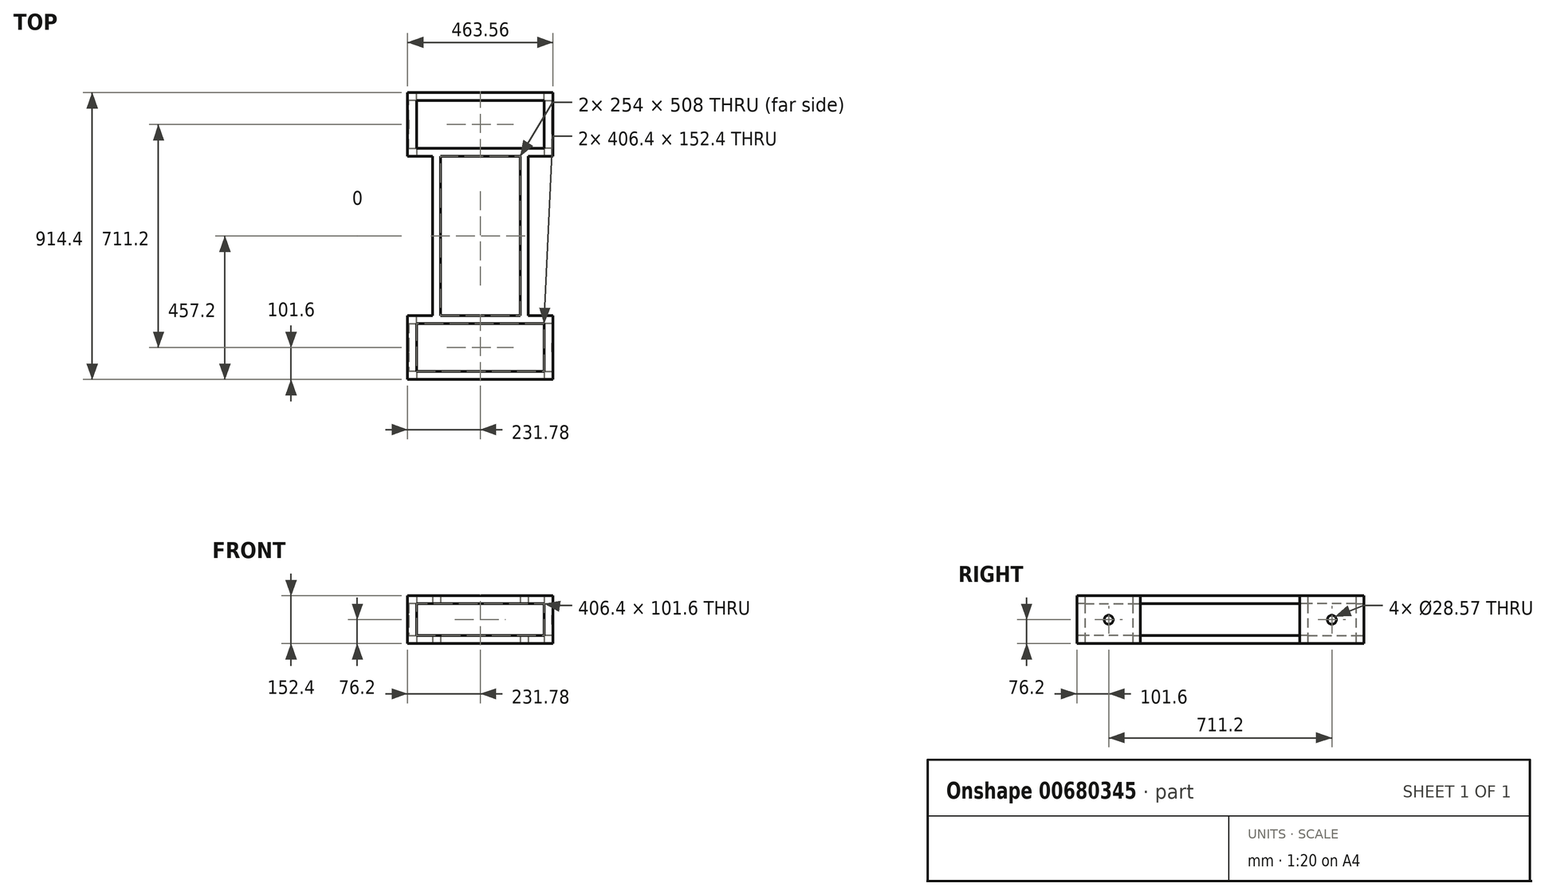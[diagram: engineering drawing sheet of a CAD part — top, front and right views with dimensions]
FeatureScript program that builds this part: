
annotation { "Feature Type Name" : "Feature", "Feature Type Description" : "" }
export const myFeature = defineFeature(function(context is Context, id is Id, definition is map)
    precondition{}
    {
        {
            var Q0;
            Q0=qCreatedBy(makeId("Top.planeOp"),FACE);
            var sketch = newSketch(context, id + "F0", { "sketchPlane" : qUnion([Q0])});
            skLineSegment(sketch, "E0.bottom", {"start": v(-228.6, 457.2) * mm, "end": v(228.6, 457.2) * mm});
            skLineSegment(sketch, "E0.top", {"start": v(-228.6, -457.2) * mm, "end": v(228.6, -457.2) * mm});
            skLineSegment(sketch, "E0.left", {"start": v(-228.6, 457.2) * mm, "end": v(-228.6, -457.2) * mm, "construction": true});
            skLineSegment(sketch, "E0.right", {"start": v(228.6, 457.2) * mm, "end": v(228.6, -457.2) * mm, "construction": true});
            skLineSegment(sketch, "E1.bottom", {"start": v(-203.2, 431.8) * mm, "end": v(203.2, 431.8) * mm});
            skLineSegment(sketch, "E1.top", {"start": v(-203.2, -431.8) * mm, "end": v(203.2, -431.8) * mm});
            skLineSegment(sketch, "E1.left", {"start": v(-203.2, 431.8) * mm, "end": v(-203.2, -431.8) * mm, "construction": true});
            skLineSegment(sketch, "E1.right", {"start": v(203.2, 431.8) * mm, "end": v(203.2, -431.8) * mm, "construction": true});
            skPoint(sketch, "E2", {"position": v(0, 431.8) * mm});
            skPoint(sketch, "E3", {"position": v(0, 457.2) * mm});
            skPoint(sketch, "E4", {"position": v(228.6, 0) * mm});
            skPoint(sketch, "E5", {"position": v(203.2, 0) * mm});
            skLineSegment(sketch, "E6.bottom", {"start": v(-203.2, -279.4) * mm, "end": v(203.2, -279.4) * mm});
            skLineSegment(sketch, "E6.top", {"start": v(-203.2, -254) * mm, "end": v(203.2, -254) * mm});
            skLineSegment(sketch, "E6.left", {"start": v(-203.2, -279.4) * mm, "end": v(-203.2, -254) * mm});
            skLineSegment(sketch, "E6.right", {"start": v(203.2, -279.4) * mm, "end": v(203.2, -254) * mm});
            skLineSegment(sketch, "E7.MirrorCS", {"start": v(-203.2, 254) * mm, "end": v(203.2, 254) * mm});
            skLineSegment(sketch, "E8.MirrorCS", {"start": v(-203.2, 279.4) * mm, "end": v(203.2, 279.4) * mm});
            skLineSegment(sketch, "E9", {"start": v(0, 457.2) * mm, "end": v(0, -457.2) * mm, "construction": true});
            skLineSegment(sketch, "E10.bottom", {"start": v(-152.4, -254) * mm, "end": v(-127, -254) * mm});
            skLineSegment(sketch, "E10.top", {"start": v(-152.4, 254) * mm, "end": v(-127, 254) * mm});
            skLineSegment(sketch, "E10.left", {"start": v(-152.4, -254) * mm, "end": v(-152.4, 254) * mm});
            skLineSegment(sketch, "E10.right", {"start": v(-127, -254) * mm, "end": v(-127, 254) * mm});
            skLineSegment(sketch, "E11.MirrorCS", {"start": v(127, -254) * mm, "end": v(127, 254) * mm});
            skLineSegment(sketch, "E12.MirrorCS", {"start": v(152.4, -254) * mm, "end": v(152.4, 254) * mm});
            skLineSegment(sketch, "E13", {"start": v(-203.2, 254) * mm, "end": v(-228.6, 254) * mm});
            skLineSegment(sketch, "E14", {"start": v(-228.6, 254) * mm, "end": v(-228.6, 457.2) * mm});
            skLineSegment(sketch, "E15", {"start": v(-203.2, 431.8) * mm, "end": v(-203.2, 279.4) * mm});
            skLineSegment(sketch, "E16", {"start": v(-203.2, -254) * mm, "end": v(-228.6, -254) * mm});
            skLineSegment(sketch, "E17", {"start": v(-228.6, -254) * mm, "end": v(-228.6, -457.2) * mm});
            skLineSegment(sketch, "E18", {"start": v(-203.2, -431.8) * mm, "end": v(-203.2, -279.4) * mm});
            skLineSegment(sketch, "E19", {"start": v(203.2, -431.8) * mm, "end": v(203.2, -279.4) * mm});
            skLineSegment(sketch, "E20", {"start": v(203.2, -254) * mm, "end": v(228.6, -254) * mm});
            skLineSegment(sketch, "E21", {"start": v(228.6, -254) * mm, "end": v(228.6, -457.2) * mm});
            skLineSegment(sketch, "E22", {"start": v(203.2, 254) * mm, "end": v(228.6, 254) * mm});
            skLineSegment(sketch, "E23", {"start": v(228.6, 254) * mm, "end": v(228.6, 457.2) * mm});
            skLineSegment(sketch, "E24", {"start": v(203.2, 279.4) * mm, "end": v(203.2, 431.8) * mm});
            skSolve(sketch);
        }
        {
            var Q0;
            Q0=qSketchRegion(id+"F0",true);
            var Q1;
            Q1=makeQuery(id+"F0.imprint","IMPRINT",FACE,{"disambiguationData":[TD([[makeQuery(id+"F0.imprint","IMPRINT",EDGE,{"derivedFrom":sQuery(id+"F0.wireOp",EDGE,"E6.bottom")}),1.0]])]});
            var Q2;
            {var subQ0=sQuery(id+"F0.wireOp",EDGE,"E7.MirrorCS");Q2=makeQuery(id+"F0.imprint","IMPRINT",FACE,{"disambiguationData":[TD([[makeQuery(id+"F0.imprint","IMPRINT",EDGE,{"derivedFrom":subQ0}),1.0]])]});}
            extrude(context, id + "F1", {"entities" : qUnion([Q0, Q1, Q2]), "depth" : 25.4 * mm, "offsetDistance" : 25.4 * mm});
        }
        {
            var Q0;
            Q0=makeQuery(id+"F1.opExtrude","CAP_FACE",FACE,{"disambiguationData":[OSD([sQuery(id+"F0.wireOp",EDGE,"E0.bottom"),sQuery(id+"F0.wireOp",EDGE,"E0.top"),sQuery(id+"F0.wireOp",EDGE,"E0.left"),sQuery(id+"F0.wireOp",EDGE,"E0.right"),sQuery(id+"F0.wireOp",EDGE,"E1.bottom"),sQuery(id+"F0.wireOp",EDGE,"E1.top"),sQuery(id+"F0.wireOp",EDGE,"E1.left"),sQuery(id+"F0.wireOp",EDGE,"E1.right")])],"isStart":false});
            var sketch = newSketch(context, id + "F2", { "sketchPlane" : qUnion([Q0])});
            skLineSegment(sketch, "E25.bottom", {"start": v(-203.2, -431.8) * mm, "end": v(-228.6, -431.8) * mm});
            skLineSegment(sketch, "E25.top", {"start": v(-203.2, -457.2) * mm, "end": v(-228.6, -457.2) * mm});
            skLineSegment(sketch, "E25.left", {"start": v(-203.2, -431.8) * mm, "end": v(-203.2, -457.2) * mm});
            skLineSegment(sketch, "E25.right", {"start": v(-228.6, -431.8) * mm, "end": v(-228.6, -457.2) * mm});
            skLineSegment(sketch, "E26.MirrorCS", {"start": v(-228.6, 431.8) * mm, "end": v(-228.6, 457.2) * mm});
            skLineSegment(sketch, "E27.MirrorCS", {"start": v(-203.2, 431.8) * mm, "end": v(-203.2, 457.2) * mm});
            skLineSegment(sketch, "E28.MirrorCS", {"start": v(-203.2, 457.2) * mm, "end": v(-228.6, 457.2) * mm});
            skLineSegment(sketch, "E29.MirrorCS", {"start": v(-203.2, 431.8) * mm, "end": v(-228.6, 431.8) * mm});
            skLineSegment(sketch, "E30.MirrorCS", {"start": v(203.2, 457.2) * mm, "end": v(228.6, 457.2) * mm});
            skLineSegment(sketch, "E31.MirrorCS", {"start": v(203.2, 431.8) * mm, "end": v(203.2, 457.2) * mm});
            skLineSegment(sketch, "E32.MirrorCS", {"start": v(228.6, 431.8) * mm, "end": v(228.6, 457.2) * mm});
            skLineSegment(sketch, "E33.MirrorCS", {"start": v(228.6, -431.8) * mm, "end": v(228.6, -457.2) * mm});
            skLineSegment(sketch, "E34.MirrorCS", {"start": v(203.2, -431.8) * mm, "end": v(203.2, -457.2) * mm});
            skLineSegment(sketch, "E35.MirrorCS", {"start": v(203.2, -457.2) * mm, "end": v(228.6, -457.2) * mm});
            skLineSegment(sketch, "E36.MirrorCS", {"start": v(203.2, -431.8) * mm, "end": v(228.6, -431.8) * mm});
            skLineSegment(sketch, "E37.MirrorCS", {"start": v(203.2, 431.8) * mm, "end": v(228.6, 431.8) * mm});
            skLineSegment(sketch, "E38.bottom", {"start": v(-228.6, -279.4) * mm, "end": v(-203.2, -279.4) * mm});
            skLineSegment(sketch, "E38.top", {"start": v(-228.6, -254) * mm, "end": v(-203.2, -254) * mm});
            skLineSegment(sketch, "E38.left", {"start": v(-228.6, -279.4) * mm, "end": v(-228.6, -254) * mm});
            skLineSegment(sketch, "E38.right", {"start": v(-203.2, -279.4) * mm, "end": v(-203.2, -254) * mm});
            skLineSegment(sketch, "E39.MirrorCS", {"start": v(-228.6, 279.4) * mm, "end": v(-228.6, 254) * mm});
            skLineSegment(sketch, "E40.MirrorCS", {"start": v(-228.6, 279.4) * mm, "end": v(-203.2, 279.4) * mm});
            skLineSegment(sketch, "E41.MirrorCS", {"start": v(-203.2, 279.4) * mm, "end": v(-203.2, 254) * mm});
            skLineSegment(sketch, "E42.MirrorCS", {"start": v(-228.6, 254) * mm, "end": v(-203.2, 254) * mm});
            skLineSegment(sketch, "E43.MirrorCS", {"start": v(228.6, -254) * mm, "end": v(203.2, -254) * mm});
            skLineSegment(sketch, "E44.MirrorCS", {"start": v(203.2, -279.4) * mm, "end": v(203.2, -254) * mm});
            skLineSegment(sketch, "E45.MirrorCS", {"start": v(228.6, 279.4) * mm, "end": v(203.2, 279.4) * mm});
            skLineSegment(sketch, "E46.MirrorCS", {"start": v(228.6, 254) * mm, "end": v(203.2, 254) * mm});
            skLineSegment(sketch, "E47.MirrorCS", {"start": v(203.2, 279.4) * mm, "end": v(203.2, 254) * mm});
            skLineSegment(sketch, "E48.MirrorCS", {"start": v(228.6, 279.4) * mm, "end": v(228.6, 254) * mm});
            skLineSegment(sketch, "E49.MirrorCS", {"start": v(228.6, -279.4) * mm, "end": v(203.2, -279.4) * mm});
            skLineSegment(sketch, "E50.MirrorCS", {"start": v(228.6, -279.4) * mm, "end": v(228.6, -254) * mm});
            skSolve(sketch);
        }
        {
            var Q0;
            Q0=qSketchRegion(id+"F2",true);
            extrude(context, id + "F3", {"entities" : qUnion([Q0]), "operationType" : NewBodyOperationType.ADD, "depth" : 101.6 * mm, "offsetDistance" : 25.4 * mm});
        }
        {
            var Q0;
            Q0=makeQuery(id+"F3.opExtrude","CAP_FACE",FACE,{"disambiguationData":[OSD([sQuery(id+"F2.wireOp",EDGE,"E33.MirrorCS"),sQuery(id+"F2.wireOp",EDGE,"E34.MirrorCS"),sQuery(id+"F2.wireOp",EDGE,"E35.MirrorCS"),sQuery(id+"F2.wireOp",EDGE,"E36.MirrorCS")])],"isStart":false});
            var sketch = newSketch(context, id + "F4", { "sketchPlane" : qUnion([Q0])});
            skLineSegment(sketch, "E51.bottom", {"start": v(228.6, 457.2) * mm, "end": v(-228.6, 457.2) * mm});
            skLineSegment(sketch, "E51.top", {"start": v(228.6, 431.8) * mm, "end": v(-228.6, 431.8) * mm});
            skLineSegment(sketch, "E51.left", {"start": v(228.6, 457.2) * mm, "end": v(228.6, 431.8) * mm});
            skLineSegment(sketch, "E51.right", {"start": v(-228.6, 457.2) * mm, "end": v(-228.6, 431.8) * mm});
            skLineSegment(sketch, "E52.bottom", {"start": v(228.6, 431.8) * mm, "end": v(203.2, 431.8) * mm});
            skLineSegment(sketch, "E52.top", {"start": v(228.6, 254) * mm, "end": v(203.2, 254) * mm});
            skLineSegment(sketch, "E52.left", {"start": v(228.6, 431.8) * mm, "end": v(228.6, 254) * mm});
            skLineSegment(sketch, "E52.right", {"start": v(203.2, 431.8) * mm, "end": v(203.2, 254) * mm});
            skLineSegment(sketch, "E53.MirrorCS", {"start": v(-203.2, 431.8) * mm, "end": v(-203.2, 254) * mm});
            skLineSegment(sketch, "E54.MirrorCS", {"start": v(-228.6, 431.8) * mm, "end": v(-228.6, 254) * mm});
            skLineSegment(sketch, "E55.MirrorCS", {"start": v(-228.6, 254) * mm, "end": v(-203.2, 254) * mm});
            skLineSegment(sketch, "E56.bottom", {"start": v(203.2, 254) * mm, "end": v(-203.2, 254) * mm});
            skLineSegment(sketch, "E56.top", {"start": v(203.2, 279.4) * mm, "end": v(-203.2, 279.4) * mm});
            skLineSegment(sketch, "E56.left", {"start": v(203.2, 254) * mm, "end": v(203.2, 279.4) * mm});
            skLineSegment(sketch, "E56.right", {"start": v(-203.2, 254) * mm, "end": v(-203.2, 279.4) * mm});
            skLineSegment(sketch, "E57.bottom", {"start": v(152.4, 254) * mm, "end": v(127, 254) * mm});
            skLineSegment(sketch, "E57.top", {"start": v(152.4, -254) * mm, "end": v(127, -254) * mm});
            skLineSegment(sketch, "E57.left", {"start": v(152.4, 254) * mm, "end": v(152.4, -254) * mm});
            skLineSegment(sketch, "E57.right", {"start": v(127, 254) * mm, "end": v(127, -254) * mm});
            skLineSegment(sketch, "E58.MirrorCS", {"start": v(-152.4, 254) * mm, "end": v(-152.4, -254) * mm});
            skLineSegment(sketch, "E59.MirrorCS", {"start": v(-127, 254) * mm, "end": v(-127, -254) * mm});
            skLineSegment(sketch, "E60.MirrorCS", {"start": v(228.6, -431.8) * mm, "end": v(203.2, -431.8) * mm});
            skLineSegment(sketch, "E61.MirrorCS", {"start": v(-228.6, -457.2) * mm, "end": v(-228.6, -431.8) * mm});
            skLineSegment(sketch, "E62.MirrorCS", {"start": v(228.6, -457.2) * mm, "end": v(228.6, -431.8) * mm});
            skLineSegment(sketch, "E63.MirrorCS", {"start": v(228.6, -254) * mm, "end": v(203.2, -254) * mm});
            skLineSegment(sketch, "E64.MirrorCS", {"start": v(-228.6, -254) * mm, "end": v(-203.2, -254) * mm});
            skLineSegment(sketch, "E65.MirrorCS", {"start": v(203.2, -254) * mm, "end": v(203.2, -279.4) * mm});
            skLineSegment(sketch, "E66.MirrorCS", {"start": v(-203.2, -254) * mm, "end": v(-203.2, -279.4) * mm});
            skLineSegment(sketch, "E67.MirrorCS", {"start": v(228.6, -457.2) * mm, "end": v(-228.6, -457.2) * mm});
            skLineSegment(sketch, "E68.MirrorCS", {"start": v(203.2, -431.8) * mm, "end": v(203.2, -254) * mm});
            skLineSegment(sketch, "E69.MirrorCS", {"start": v(203.2, -254) * mm, "end": v(-203.2, -254) * mm});
            skLineSegment(sketch, "E70.MirrorCS", {"start": v(203.2, -279.4) * mm, "end": v(-203.2, -279.4) * mm});
            skLineSegment(sketch, "E71.MirrorCS", {"start": v(-228.6, -431.8) * mm, "end": v(-228.6, -254) * mm});
            skLineSegment(sketch, "E72.MirrorCS", {"start": v(-203.2, -431.8) * mm, "end": v(-203.2, -254) * mm});
            skLineSegment(sketch, "E73.MirrorCS", {"start": v(228.6, -431.8) * mm, "end": v(-228.6, -431.8) * mm});
            skLineSegment(sketch, "E74.MirrorCS", {"start": v(228.6, -431.8) * mm, "end": v(228.6, -254) * mm});
            skSolve(sketch);
        }
        {
            var Q0;
            Q0=qSketchRegion(id+"F4",true);
            extrude(context, id + "F5", {"entities" : qUnion([Q0]), "operationType" : NewBodyOperationType.ADD, "depth" : 25.4 * mm, "offsetDistance" : 25.4 * mm});
        }
        {
            var Q0;
            Q0=makeQuery(id+"F5.boolean.opBoolean","MERGE",FACE,{"derivedFrom":[makeQuery(id+"F3.boolean.opBoolean","MERGE",FACE,{"derivedFrom":[makeQuery(id+"F1.opExtrude","SWEPT_FACE",FACE,{"disambiguationData":[OSD([sQuery(id+"F0.wireOp",EDGE,"E0.right")])]}),makeQuery(id+"F3.opExtrude","SWEPT_FACE",FACE,{"disambiguationData":[OSD([sQuery(id+"F2.wireOp",EDGE,"E32.MirrorCS")])]}),makeQuery(id+"F3.opExtrude","SWEPT_FACE",FACE,{"disambiguationData":[OSD([sQuery(id+"F2.wireOp",EDGE,"E33.MirrorCS")])]}),makeQuery(id+"F3.opExtrude","SWEPT_FACE",FACE,{"disambiguationData":[OSD([sQuery(id+"F2.wireOp",EDGE,"E48.MirrorCS")])]}),makeQuery(id+"F3.opExtrude","SWEPT_FACE",FACE,{"disambiguationData":[OSD([sQuery(id+"F2.wireOp",EDGE,"E50.MirrorCS")])]})]}),makeQuery(id+"F5.opExtrude","SWEPT_FACE",FACE,{"disambiguationData":[OSD([sQuery(id+"F4.wireOp",EDGE,"Wdg1V6kY-x6Q8-cJW5-QTke-MaLvcnpzVtc4.right")])]})]});
            var sketch = newSketch(context, id + "F6", { "sketchPlane" : qUnion([Q0])});
            skLineSegment(sketch, "E75.bottom", {"start": v(-457.2, 152.4) * mm, "end": v(-254, 152.4) * mm});
            skLineSegment(sketch, "E75.top", {"start": v(-457.2, 0) * mm, "end": v(-254, 0) * mm});
            skLineSegment(sketch, "E75.left", {"start": v(-457.2, 152.4) * mm, "end": v(-457.2, 0) * mm});
            skLineSegment(sketch, "E75.right", {"start": v(-254, 152.4) * mm, "end": v(-254, 0) * mm});
            skLineSegment(sketch, "E76.MirrorCS", {"start": v(457.2, 152.4) * mm, "end": v(254, 152.4) * mm});
            skLineSegment(sketch, "E77.MirrorCS", {"start": v(457.2, 0) * mm, "end": v(254, 0) * mm});
            skLineSegment(sketch, "E78.MirrorCS", {"start": v(457.2, 152.4) * mm, "end": v(457.2, 0) * mm});
            skLineSegment(sketch, "E79.MirrorCS", {"start": v(254, 152.4) * mm, "end": v(254, 0) * mm});
            skSolve(sketch);
        }
        {
            var Q0;
            Q0=qSketchRegion(id+"F6",true);
            extrude(context, id + "F7", {"entities" : qUnion([Q0]), "operationType" : NewBodyOperationType.ADD, "depth" : 3.17 * mm, "offsetDistance" : 25.4 * mm});
        }
        {
            var Q0;
            Q0=makeQuery(id+"F5.boolean.opBoolean","MERGE",FACE,{"derivedFrom":[makeQuery(id+"F3.boolean.opBoolean","MERGE",FACE,{"derivedFrom":[makeQuery(id+"F1.opExtrude","SWEPT_FACE",FACE,{"disambiguationData":[OSD([sQuery(id+"F0.wireOp",EDGE,"E0.left")])]}),makeQuery(id+"F3.opExtrude","SWEPT_FACE",FACE,{"disambiguationData":[OSD([sQuery(id+"F2.wireOp",EDGE,"E25.right")])]}),makeQuery(id+"F3.opExtrude","SWEPT_FACE",FACE,{"disambiguationData":[OSD([sQuery(id+"F2.wireOp",EDGE,"E26.MirrorCS")])]}),makeQuery(id+"F3.opExtrude","SWEPT_FACE",FACE,{"disambiguationData":[OSD([sQuery(id+"F2.wireOp",EDGE,"E38.left")])]}),makeQuery(id+"F3.opExtrude","SWEPT_FACE",FACE,{"disambiguationData":[OSD([sQuery(id+"F2.wireOp",EDGE,"E39.MirrorCS")])]})]}),makeQuery(id+"F5.opExtrude","SWEPT_FACE",FACE,{"disambiguationData":[OSD([sQuery(id+"F4.wireOp",EDGE,"Wdg1V6kY-x6Q8-cJW5-QTke-MaLvcnpzVtc4.left")])]})]});
            var sketch = newSketch(context, id + "F8", { "sketchPlane" : qUnion([Q0])});
            skLineSegment(sketch, "E80.bottom", {"start": v(-457.2, 152.4) * mm, "end": v(-254, 152.4) * mm});
            skLineSegment(sketch, "E80.top", {"start": v(-457.2, 0) * mm, "end": v(-254, 0) * mm});
            skLineSegment(sketch, "E80.left", {"start": v(-457.2, 152.4) * mm, "end": v(-457.2, 0) * mm});
            skLineSegment(sketch, "E80.right", {"start": v(-254, 152.4) * mm, "end": v(-254, 0) * mm});
            skLineSegment(sketch, "E81.MirrorCS", {"start": v(457.2, 152.4) * mm, "end": v(254, 152.4) * mm});
            skLineSegment(sketch, "E82.MirrorCS", {"start": v(457.2, 0) * mm, "end": v(254, 0) * mm});
            skLineSegment(sketch, "E83.MirrorCS", {"start": v(254, 152.4) * mm, "end": v(254, 0) * mm});
            skLineSegment(sketch, "E84.MirrorCS", {"start": v(457.2, 152.4) * mm, "end": v(457.2, 0) * mm});
            skSolve(sketch);
        }
        {
            var Q0;
            Q0=qSketchRegion(id+"F8",true);
            extrude(context, id + "F9", {"entities" : qUnion([Q0]), "operationType" : NewBodyOperationType.ADD, "depth" : 3.17 * mm, "offsetDistance" : 25.4 * mm});
        }
        {
            var Q0;
            Q0=makeQuery(id+"F7.opExtrude","CAP_FACE",FACE,{"disambiguationData":[OSD([sQuery(id+"F6.wireOp",EDGE,"E76.MirrorCS"),sQuery(id+"F6.wireOp",EDGE,"E77.MirrorCS"),sQuery(id+"F6.wireOp",EDGE,"E78.MirrorCS"),sQuery(id+"F6.wireOp",EDGE,"E79.MirrorCS")])],"isStart":false});
            var sketch = newSketch(context, id + "F10", { "sketchPlane" : qUnion([Q0])});
            skLineSegment(sketch, "E85", {"start": v(457.2, 76.2) * mm, "end": v(254, 76.2) * mm, "construction": true});
            skCircle(sketch, "E86", {"center": v(355.6, 76.2) * mm, "radius": 14.29 * mm});
            skPoint(sketch, "E87.MirrorP", {"position": v(-355.6, 76.2) * mm});
            skCircle(sketch, "E88.MirrorC", {"center": v(-355.6, 76.2) * mm, "radius": 14.29 * mm});
            skLineSegment(sketch, "E89.MirrorCS", {"start": v(-457.2, 76.2) * mm, "end": v(-254, 76.2) * mm, "construction": true});
            skSolve(sketch);
        }
        {
            var Q0;
            Q0=qSketchRegion(id+"F10",true);
            extrude(context, id + "F11", {"entities" : qUnion([Q0]), "operationType" : NewBodyOperationType.REMOVE, "endBound" : BoundingType.THROUGH_ALL, "oppositeDirection" : true, "depth" : 25.4 * mm, "offsetDistance" : 25.4 * mm});
        }
    });
